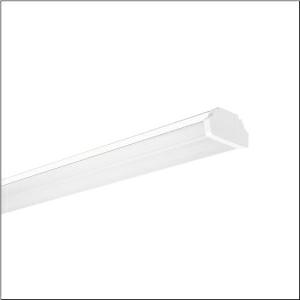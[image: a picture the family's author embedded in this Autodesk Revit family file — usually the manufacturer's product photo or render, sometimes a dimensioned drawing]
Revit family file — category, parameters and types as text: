
# Revit family: dus_r__31_mo_53bd81271v4080_fa57
name_source: partatom
category: Lighting Fixtures
units: mm (PartAtom-declared; Revit-internal decimal feet)

## family parameters
Cut with Voids When Loaded = No
Host = Face
Light Source = No
Part Type = Normal
Room Calculation Point = No
Round Connector Dimension = Use Diameter
Shared = No

## types (1)
- DUS® 31 MO (1 x LED, 7810 lm, 50.8 W, 4000K)
    Apparent Load = 51 VA
    CIE Flux Codes = 47 80 95 92 100
    Color Rendering = 80
    Color Temperature = 4000K
    Default Elevation = 1800 mm
    Description = DUS® 31 MO, luminaire insert, of sheet steel, coil coated, white, length: 1.535mm, width: 81mm, height: 90mm, 5x system unit, system units: 307mm, LED rated luminous flux: 7.810lm, light colour: 840, control gear: ON/OFF, control gear: ECG, with plug, 3-pole, with phase selection, mains connection: 220..240V, AC, 50/60Hz, rated input power: 51W, through-wiring accessed according to module size, primary optical cover: cover, of PMMA, light emission: direct distribution, primary light characteristic: symmetric, protection rating (complete): IP20, protection rating (LED compartment): IP50, insulation class (complete): insulation class I (protective earthing), certification: CE, ENEC, VDE, UKCA, impact resistance: IK03, permissible ambient temperature for indoor applications: -35..+35°C, corresponds to IFS (International Featured Standards) requirements for safety and quality in the food industry, reducing of maximum allowable ambient temperature of 5°C with ceiling mounting, packaging unit: 1 piece
    Height = 95 mm
    Lamp = 1 x LED
    Lamp Light Flux = 7810 lm
    Lamp Power = 50.8 W
    Lamp count = 1
    Length = 1535 mm
    Luminous efficacy = 154 lm/W
    Manufacturer = Siteco
    ModVariant = No
    Model = 53BD81271V4080
    Mounting Place = Ceiling
    Mounting Type = Pendant
    Number of Poles = 1
    OnlyDefault = Yes
    Power Factor = 1
    Product Name = DUS® 31 MO
    Product group = luminaire insert
    ProductGroupID = 901
    Protection Class = Protection class I
    Protection Degree = IP 20
    RLX_Detail_Level = 1
    RLX_Emergency_Light_Flux = 0 lm
    RLX_Emergency_Type = 0
    RLX_Emergency_Type_DB = No
    RlxData = <blob elided: 38677 chars, md5=13aa032b>
    Socket = socket
    Standby Power = 0 W
    System Light Flux = 7810 lm
    System Power = 51 W
    Type Comments = Product without accessories
    Type Image = l_1003451.jpg
    URL = http://relux.com
    VarID = ---
    Voltage = 0 V
    Weight = 0.00 kg
    Width = 81 mm

## geometry (parser evidence)
native form markers: Blend x4, Sweep x11
no freeform markers — native parametric forms only
